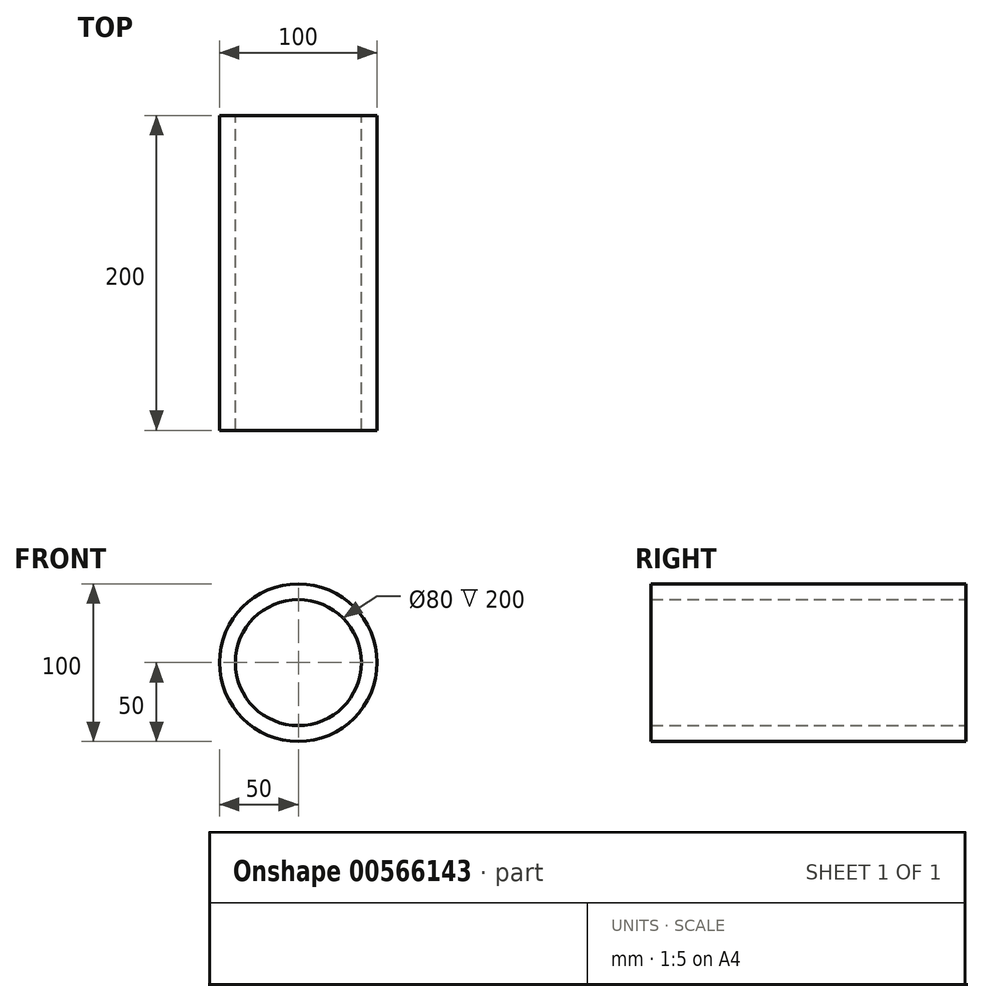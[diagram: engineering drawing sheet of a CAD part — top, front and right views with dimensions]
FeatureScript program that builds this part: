
annotation { "Feature Type Name" : "Feature", "Feature Type Description" : "" }
export const myFeature = defineFeature(function(context is Context, id is Id, definition is map)
    precondition{}
    {
        {
            var Q0;
            Q0=qCreatedBy(makeId("Front.planeOp"),FACE);
            var sketch = newSketch(context, id + "F0", { "sketchPlane" : qUnion([Q0])});
            skCircle(sketch, "E0", {"center": v(0, 0) * mm, "radius": 40 * mm});
            skCircle(sketch, "E1", {"center": v(0, 0) * mm, "radius": 50 * mm});
            skSolve(sketch);
        }
        {
            var Q0;
            Q0=makeQuery(id+"F0.imprint","IMPRINT",FACE,{"disambiguationData":[TD([[makeQuery(id+"F0.imprint","IMPRINT",EDGE,{"derivedFrom":sQuery(id+"F0.wireOp",EDGE,"E0")}),-1.0]])]});
            extrude(context, id + "F1", {"entities" : qUnion([Q0]), "endBound" : BoundingType.SYMMETRIC, "depth" : 200 * mm, "offsetDistance" : 25.4 * mm});
        }
    });
